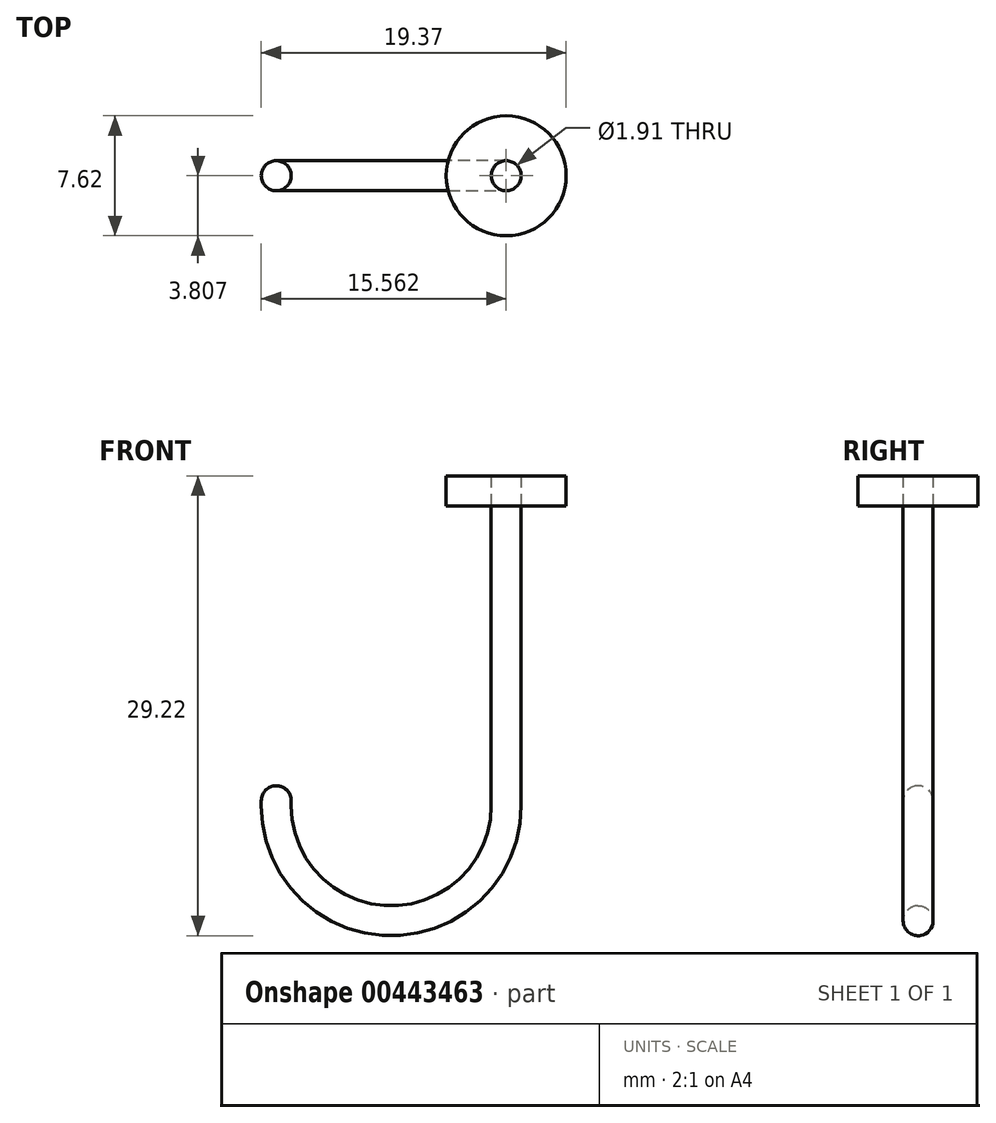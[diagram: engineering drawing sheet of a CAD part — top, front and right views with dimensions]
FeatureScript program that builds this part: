
annotation { "Feature Type Name" : "Feature", "Feature Type Description" : "" }
export const myFeature = defineFeature(function(context is Context, id is Id, definition is map)
    precondition{}
    {
        {
            var Q0;
            Q0=qCreatedBy(makeId("Front.planeOp"),FACE);
            var sketch = newSketch(context, id + "F0", { "sketchPlane" : qUnion([Q0])});
            skLineSegment(sketch, "E0", {"start": v(0, 38.1) * mm, "end": v(0, 19.05) * mm});
            skLineSegment(sketch, "E1", {"start": v(-6.35, 12.7) * mm, "end": v(-6.35, 12.7) * mm});
            skLineSegment(sketch, "E2", {"start": v(-12.7, 19.05) * mm, "end": v(-12.7, 20.32) * mm});
            skPoint(sketch, "E3.visualSharp", {"position": v(-12.7, 12.7) * mm});
            skArc(sketch, "E3.filletArc", {"start": v(-12.7, 19.05) * mm, "mid": v(-10.84, 14.56) * mm, "end": v(-6.35, 12.7) * mm});
            skPoint(sketch, "E4.visualSharp", {"position": v(0, 12.7) * mm});
            skArc(sketch, "E4.filletArc", {"start": v(-6.35, 12.7) * mm, "mid": v(-1.86, 14.56) * mm, "end": v(0, 19.05) * mm});
            skLineSegment(sketch, "E5.0", {"start": v(1.9, 38.1) * mm, "end": v(1.9, 19.05) * mm});
            skArc(sketch, "E5.1", {"start": v(-6.35, 10.8) * mm, "mid": v(-0.51, 13.21) * mm, "end": v(1.9, 19.05) * mm});
            skArc(sketch, "E5.2", {"start": v(-14.6, 19.05) * mm, "mid": v(-12.19, 13.21) * mm, "end": v(-6.35, 10.8) * mm});
            skLineSegment(sketch, "E5.3", {"start": v(-14.6, 19.05) * mm, "end": v(-14.6, 20.32) * mm});
            skLineSegment(sketch, "E6", {"start": v(-14.6, 20.32) * mm, "end": v(-12.7, 20.32) * mm});
            skLineSegment(sketch, "E7", {"start": v(0, 38.1) * mm, "end": v(1.9, 38.1) * mm});
            skSolve(sketch);
        }
        {
            var Q0;
            Q0=makeQuery(id+"F0.imprint","IMPRINT",FACE,{"disambiguationData":[TD([[makeQuery(id+"F0.imprint","IMPRINT",EDGE,{"derivedFrom":sQuery(id+"F0.wireOp",EDGE,"E0")}),1.0]])]});
            extrude(context, id + "F1", {"entities" : qUnion([Q0]), "depth" : 1.9 * mm});
        }
        {
            var Q0;
            Q0=makeQuery(id+"F1.opExtrude","CAP_EDGE",EDGE,{"disambiguationData":[OSD([sQuery(id+"F0.wireOp",EDGE,"E5.0")])],"isStart":false});
            var Q1;
            Q1=makeQuery(id+"F1.opExtrude","CAP_EDGE",EDGE,{"disambiguationData":[OSD([sQuery(id+"F0.wireOp",EDGE,"E0")])],"isStart":false});
            var Q2;
            Q2=makeQuery(id+"F1.opExtrude","CAP_EDGE",EDGE,{"disambiguationData":[OSD([sQuery(id+"F0.wireOp",EDGE,"E5.0")])],"isStart":true});
            var Q3;
            Q3=makeQuery(id+"F1.opExtrude","CAP_EDGE",EDGE,{"disambiguationData":[OSD([sQuery(id+"F0.wireOp",EDGE,"E3.filletArc"),sQuery(id+"F0.wireOp",EDGE,"E4.filletArc")])],"isStart":true});
            fillet(context, id + "F2", {"entities" : qUnion([Q0, Q1, Q2, Q3]), "radius" : 0.95 * mm, "tangentPropagation" : true, "allowEdgeOverflow" : false});
        }
        {
            var Q0;
            Q0=makeQuery(id+"F2.opFillet","BLEND_EDGE",EDGE,{"blendedFrom":[makeQuery(id+"F1.opExtrude","CAP_EDGE",EDGE,{"disambiguationData":[OSD([sQuery(id+"F0.wireOp",EDGE,"E2")])],"isStart":true}),makeQuery(id+"F1.opExtrude","SWEPT_FACE",FACE,{"disambiguationData":[OSD([sQuery(id+"F0.wireOp",EDGE,"E6")])]})],"blendedInto":[makeQuery(id+"F1.opExtrude","SWEPT_FACE",FACE,{"disambiguationData":[OSD([sQuery(id+"F0.wireOp",EDGE,"E6")])]})]});
            fillet(context, id + "F3", {"entities" : qUnion([Q0]), "radius" : 0.95 * mm, "tangentPropagation" : true, "allowEdgeOverflow" : false});
        }
        {
            var Q0;
            Q0=makeQuery(id+"F1.opExtrude","SWEPT_FACE",FACE,{"disambiguationData":[OSD([sQuery(id+"F0.wireOp",EDGE,"E7")])]});
            var sketch = newSketch(context, id + "F4", { "sketchPlane" : qUnion([Q0])});
            skCircle(sketch, "E8", {"center": v(0.95, -0.95) * mm, "radius": 3.81 * mm});
            skSolve(sketch);
        }
        {
            var Q0;
            Q0=makeQuery(id+"F4.imprint","IMPRINT",FACE,{"disambiguationData":[TD([[makeQuery(id+"F4.imprint","IMPRINT",EDGE,{"derivedFrom":sQuery(id+"F4.wireOp",EDGE,"E8")}),1.0]])]});
            extrude(context, id + "F5", {"entities" : qUnion([Q0]), "operationType" : NewBodyOperationType.ADD, "depth" : 1.9 * mm});
        }
    });
